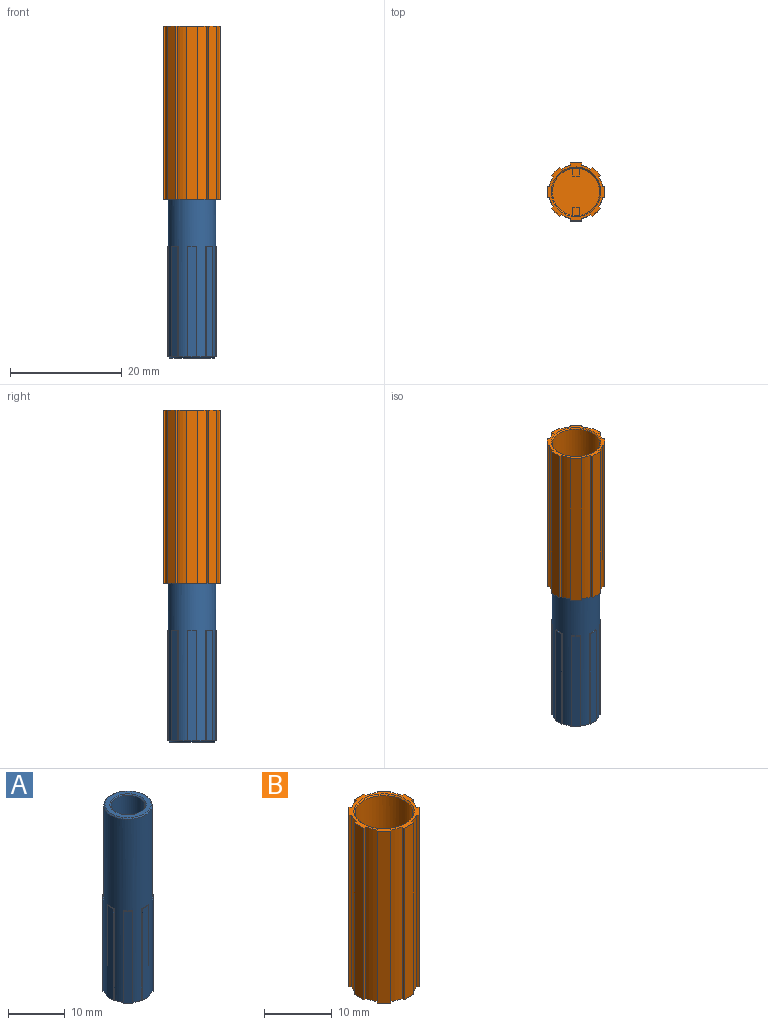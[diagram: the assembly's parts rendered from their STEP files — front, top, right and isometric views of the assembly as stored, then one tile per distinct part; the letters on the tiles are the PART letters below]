
ASSEMBLY  parts=2 mates=1
PART A: 48 faces, bbox 8.9x8.9x40 mm
  f0: cylinder r=4.28mm len=39.6mm, axis (0,0,-1), area 808.7mm2, adj f5,f7,f8,f10,f11,f13,f15,f16
  f1: plane 8.15x8.15mm, normal (0,0,1), area 20mm2, adj f6,f7
  f2: plane 8.15x8.15mm, normal (0,0,-1), area 20mm2, adj f4,f5
  f3: cylinder r=3mm len=39.6mm, axis (0,0,1), area 746.4mm2, adj f4,f6
  f4: cone r=3.2mm half-angle=45deg, axis (0,0,-1), area 5.5mm2, adj f2,f3
  f5: cone r=4.28mm half-angle=45deg, axis (0,0,1), area 7.4mm2, adj f0,f2,f9,f14,f19,f24,f29,f34
  f6: cone r=3mm half-angle=45deg, axis (0,0,1), area 5.5mm2, adj f1,f3
  f7: cone r=4.07mm half-angle=45deg, axis (0,0,-1), area 7.4mm2, adj f0,f1
  f8: plane 19.8x0.23mm, normal (0,-1,0), area 4.5mm2, adj f0,f9,f11,f12
  f9: plane 1.6x0.23mm, normal (0,0,-1), area 0.3mm2, adj f5,f8,f10,f12
  f10: plane 19.8x0.23mm, normal (0,1,0), area 4.5mm2, adj f0,f9,f11,f12
  f11: plane 1.6x0.23mm, normal (0,0,1), area 0.3mm2, adj f0,f8,f10,f12
  f12: plane 19.8x1.6mm, normal (1,0,0), area 31.7mm2, adj f8,f9,f10,f11
  f13: plane 19.8x0.16mm, normal (0.71,-0.71,0), area 4.5mm2, adj f0,f14,f16,f17
  f14: plane 1.29x1.29mm, normal (0,0,-1), area 0.3mm2, adj f5,f13,f15,f17
  f15: plane 19.8x0.16mm, normal (-0.71,0.71,0), area 4.5mm2, adj f0,f14,f16,f17
  f16: plane 1.29x1.29mm, normal (0,0,1), area 0.3mm2, adj f0,f13,f15,f17
  f17: plane 19.8x1.13mm, normal (0.71,0.71,0), area 31.7mm2, adj f13,f14,f15,f16
  f18: plane 19.8x0.23mm, normal (1,0,0), area 4.5mm2, adj f0,f19,f21,f22
  f19: plane 1.6x0.23mm, normal (0,0,-1), area 0.3mm2, adj f5,f18,f20,f22
  f20: plane 19.8x0.23mm, normal (-1,0,0), area 4.5mm2, adj f0,f19,f21,f22
  f21: plane 1.6x0.23mm, normal (0,0,1), area 0.3mm2, adj f0,f18,f20,f22
  f22: plane 19.8x1.6mm, normal (0,1,0), area 31.7mm2, adj f18,f19,f20,f21
  f23: plane 19.8x0.16mm, normal (0.71,0.71,0), area 4.5mm2, adj f0,f24,f26,f27
  f24: plane 1.29x1.29mm, normal (0,0,-1), area 0.3mm2, adj f5,f23,f25,f27
  f25: plane 19.8x0.16mm, normal (-0.71,-0.71,0), area 4.5mm2, adj f0,f24,f26,f27
  f26: plane 1.29x1.29mm, normal (0,0,1), area 0.3mm2, adj f0,f23,f25,f27
  f27: plane 19.8x1.13mm, normal (-0.71,0.71,0), area 31.7mm2, adj f23,f24,f25,f26
  f28: plane 19.8x0.23mm, normal (0,1,0), area 4.5mm2, adj f0,f29,f31,f32
  f29: plane 1.6x0.23mm, normal (0,0,-1), area 0.3mm2, adj f5,f28,f30,f32
  f30: plane 19.8x0.23mm, normal (0,-1,0), area 4.5mm2, adj f0,f29,f31,f32
  f31: plane 1.6x0.23mm, normal (0,0,1), area 0.3mm2, adj f0,f28,f30,f32
  f32: plane 19.8x1.6mm, normal (-1,0,0), area 31.7mm2, adj f28,f29,f30,f31
  f33: plane 19.8x0.16mm, normal (-0.71,0.71,0), area 4.5mm2, adj f0,f34,f36,f37
  f34: plane 1.29x1.29mm, normal (0,0,-1), area 0.3mm2, adj f5,f33,f35,f37
  f35: plane 19.8x0.16mm, normal (0.71,-0.71,0), area 4.5mm2, adj f0,f34,f36,f37
  f36: plane 1.29x1.29mm, normal (0,0,1), area 0.3mm2, adj f0,f33,f35,f37
  f37: plane 19.8x1.13mm, normal (-0.71,-0.71,0), area 31.7mm2, adj f33,f34,f35,f36
  f38: plane 19.8x0.23mm, normal (-1,0,0), area 4.5mm2, adj f0,f39,f41,f42
  f39: plane 1.6x0.23mm, normal (0,0,-1), area 0.3mm2, adj f5,f38,f40,f42
  f40: plane 19.8x0.23mm, normal (1,0,0), area 4.5mm2, adj f0,f39,f41,f42
  f41: plane 1.6x0.23mm, normal (0,0,1), area 0.3mm2, adj f0,f38,f40,f42
  f42: plane 19.8x1.6mm, normal (0,-1,0), area 31.7mm2, adj f38,f39,f40,f41
  f43: plane 19.8x0.16mm, normal (-0.71,-0.71,0), area 4.5mm2, adj f0,f44,f46,f47
  f44: plane 1.29x1.29mm, normal (0,0,-1), area 0.3mm2, adj f5,f43,f45,f47
  f45: plane 19.8x0.16mm, normal (0.71,0.71,0), area 4.5mm2, adj f0,f44,f46,f47
  f46: plane 1.29x1.29mm, normal (0,0,1), area 0.3mm2, adj f0,f43,f45,f47
  f47: plane 19.8x1.13mm, normal (0.71,-0.71,0), area 31.7mm2, adj f43,f44,f45,f46
PART B: 56 faces, bbox 10.4x10.4x31 mm
  f0: cylinder r=4.88mm len=31mm, axis (0,0,-1), area 56.3mm2, adj f11,f12,f31,f51
  f1: cylinder r=4.88mm len=31mm, axis (0,0,-1), area 56.3mm2, adj f11,f12,f48,f52
  f2: cylinder r=4.88mm len=31mm, axis (0,0,-1), area 56.3mm2, adj f11,f12,f45,f49
  f3: cylinder r=4.88mm len=31mm, axis (0,0,-1), area 56.3mm2, adj f11,f12,f42,f46
  f4: cylinder r=4.88mm len=31mm, axis (0,0,-1), area 56.3mm2, adj f11,f12,f39,f43
  f5: cylinder r=4.88mm len=31mm, axis (0,0,-1), area 56.3mm2, adj f11,f12,f36,f40
  f6: cylinder r=4.88mm len=31mm, axis (0,0,-1), area 56.3mm2, adj f11,f12,f33,f37
  f7: cylinder r=4.88mm len=31mm, axis (0,0,-1), area 56.3mm2, adj f11,f12,f30,f34
  f8: cylinder r=4.25mm len=14.41mm, axis (0,0,-1), area 377.5mm2, adj f9,f22,f24,f25,f26,f27,f29,f54
  f9: plane 8.5x8.42mm, normal (0,0,-1), area 53.4mm2, adj f8,f23,f24,f25,f27,f28,f29
  f10: plane 8.5x8.42mm, normal (0,0,1), area 53.4mm2, adj f13,f14,f15,f17,f18,f19,f21
  f11: plane 10.35x10.35mm, normal (0,0,-1), area 17.8mm2, adj f0,f1,f2,f3,f4,f5,f6,f7
  f12: plane 10.35x10.35mm, normal (0,0,1), area 17.8mm2, adj f0,f1,f2,f3,f4,f5,f6,f7
  f13: cylinder r=4.25mm len=15.19mm, axis (0,0,-1), area 398.5mm2, adj f10,f14,f16,f17,f19,f20,f21,f55
  f14: plane 3x1.36mm, normal (-1,0,0), area 4.1mm2, adj f10,f13,f15,f16
  f15: plane 3x1.2mm, normal (0,-1,0), area 3.6mm2, adj f10,f14,f16,f17
  f16: plane 1.4x1.2mm, normal (0,0,1), area 1.7mm2, adj f13,f14,f15,f17
  f17: plane 3x1.36mm, normal (1,0,0), area 4.1mm2, adj f10,f13,f15,f16
  f18: plane 3x1.2mm, normal (0,1,0), area 3.6mm2, adj f10,f19,f20,f21
  f19: plane 3x1.36mm, normal (-1,0,0), area 4.1mm2, adj f10,f13,f18,f20
  f20: plane 1.4x1.2mm, normal (0,0,1), area 1.7mm2, adj f13,f18,f19,f21
  f21: plane 3x1.36mm, normal (1,0,0), area 4.1mm2, adj f10,f13,f18,f20
  f22: plane 1.4x1.2mm, normal (0,0,-1), area 1.7mm2, adj f8,f23,f24,f25
  f23: plane 3x1.2mm, normal (0,1,0), area 3.6mm2, adj f9,f22,f24,f25
  f24: plane 3x1.36mm, normal (1,0,0), area 4.1mm2, adj f8,f9,f22,f23
  f25: plane 3x1.36mm, normal (-1,0,0), area 4.1mm2, adj f8,f9,f22,f23
  f26: plane 1.4x1.2mm, normal (0,0,-1), area 1.7mm2, adj f8,f27,f28,f29
  f27: plane 3x1.36mm, normal (1,0,0), area 4.1mm2, adj f8,f9,f26,f28
  f28: plane 3x1.2mm, normal (0,-1,0), area 3.6mm2, adj f9,f26,f27,f29
  f29: plane 3x1.36mm, normal (-1,0,0), area 4.1mm2, adj f8,f9,f26,f28
  f30: plane 31x0.4mm, normal (0,-1,0), area 12.5mm2, adj f7,f11,f12,f32
  f31: plane 31x0.4mm, normal (0,1,0), area 12.5mm2, adj f0,f11,f12,f32
  f32: plane 31x2mm, normal (-1,0,0), area 62mm2, adj f11,f12,f30,f31
  f33: plane 31x0.29mm, normal (0.71,-0.71,0), area 12.5mm2, adj f6,f11,f12,f35
  f34: plane 31x0.29mm, normal (-0.71,0.71,0), area 12.5mm2, adj f7,f11,f12,f35
  f35: plane 31x1.41mm, normal (-0.71,-0.71,0), area 62mm2, adj f11,f12,f33,f34
  f36: plane 31x0.4mm, normal (1,0,0), area 12.5mm2, adj f5,f11,f12,f38
  f37: plane 31x0.4mm, normal (-1,0,0), area 12.5mm2, adj f6,f11,f12,f38
  f38: plane 31x2mm, normal (0,-1,0), area 62mm2, adj f11,f12,f36,f37
  f39: plane 31x0.29mm, normal (0.71,0.71,0), area 12.5mm2, adj f4,f11,f12,f41
  f40: plane 31x0.29mm, normal (-0.71,-0.71,0), area 12.5mm2, adj f5,f11,f12,f41
  f41: plane 31x1.41mm, normal (0.71,-0.71,0), area 62mm2, adj f11,f12,f39,f40
  f42: plane 31x0.4mm, normal (0,1,0), area 12.5mm2, adj f3,f11,f12,f44
  f43: plane 31x0.4mm, normal (0,-1,0), area 12.5mm2, adj f4,f11,f12,f44
  f44: plane 31x2mm, normal (1,0,0), area 62mm2, adj f11,f12,f42,f43
  f45: plane 31x0.29mm, normal (-0.71,0.71,0), area 12.5mm2, adj f2,f11,f12,f47
  f46: plane 31x0.29mm, normal (0.71,-0.71,0), area 12.5mm2, adj f3,f11,f12,f47
  f47: plane 31x1.41mm, normal (0.71,0.71,0), area 62mm2, adj f11,f12,f45,f46
  f48: plane 31x0.4mm, normal (-1,0,0), area 12.5mm2, adj f1,f11,f12,f50
  f49: plane 31x0.4mm, normal (1,0,0), area 12.5mm2, adj f2,f11,f12,f50
  f50: plane 31x2mm, normal (0,1,0), area 62mm2, adj f11,f12,f48,f49
  f51: plane 31x0.29mm, normal (-0.71,-0.71,0), area 12.5mm2, adj f0,f11,f12,f53
  f52: plane 31x0.29mm, normal (0.71,0.71,0), area 12.5mm2, adj f1,f11,f12,f53
  f53: plane 31x1.41mm, normal (-0.71,0.71,0), area 62mm2, adj f11,f12,f51,f52
  f54: cone r=4.25mm half-angle=45deg, axis (0,0,-1), area 7.7mm2, adj f8,f11
  f55: cone r=4.45mm half-angle=45deg, axis (0,0,1), area 7.7mm2, adj f12,f13
PLACE A t=(-33.78,15.2,-10.76)mm
PLACE B t=(-33.78,15.2,17.63)mm
MATE planar A.f0 <-> B.f26  axis (0,0,1) through (-33.78,15.2,29.24)mm
